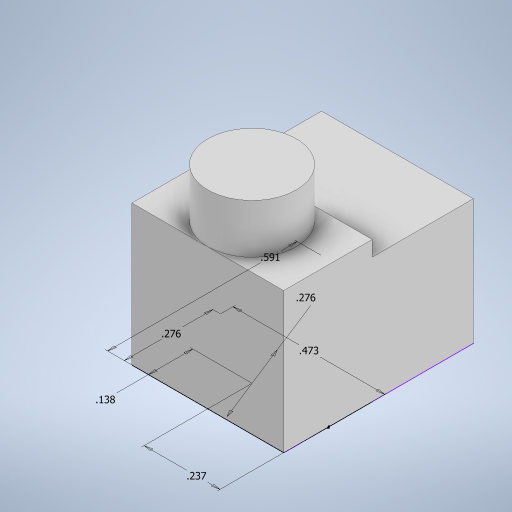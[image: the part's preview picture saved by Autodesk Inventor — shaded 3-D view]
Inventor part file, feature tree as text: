
AUTODESK INVENTOR PART (.ipt)
format: ipt  version: 2023 (Build 270158000, 158)  size: 228,864 bytes
history: native  units: in
note: dims shown in document units (in); Inventor stores cm internally (conversion verified against a paired STEP export)
features: extrude x3, sketch x1
ambient origin geometry x8: Origin, YZ Plane, XZ Plane, XY Plane, X Axis, Y Axis, Z Axis, Center Point
bodies: Solid1 (feature_tree)
feature tree (4):
  sketch  "Sketch1"  dims[d0=0.473in d1=0.276in d2=0.138in d3=0.2365in d4=0.276in d5=0.591in d6=0.39in d7=0.0in d8=0.4375in d9=0.0in d10=0.591in d11=0.0in]
  extrude  "Extrusion1"  Depth=0.276in
  extrude  "Extrusion2"  Depth=0.138in
  extrude  "Extrusion3"  Depth=0.591in
